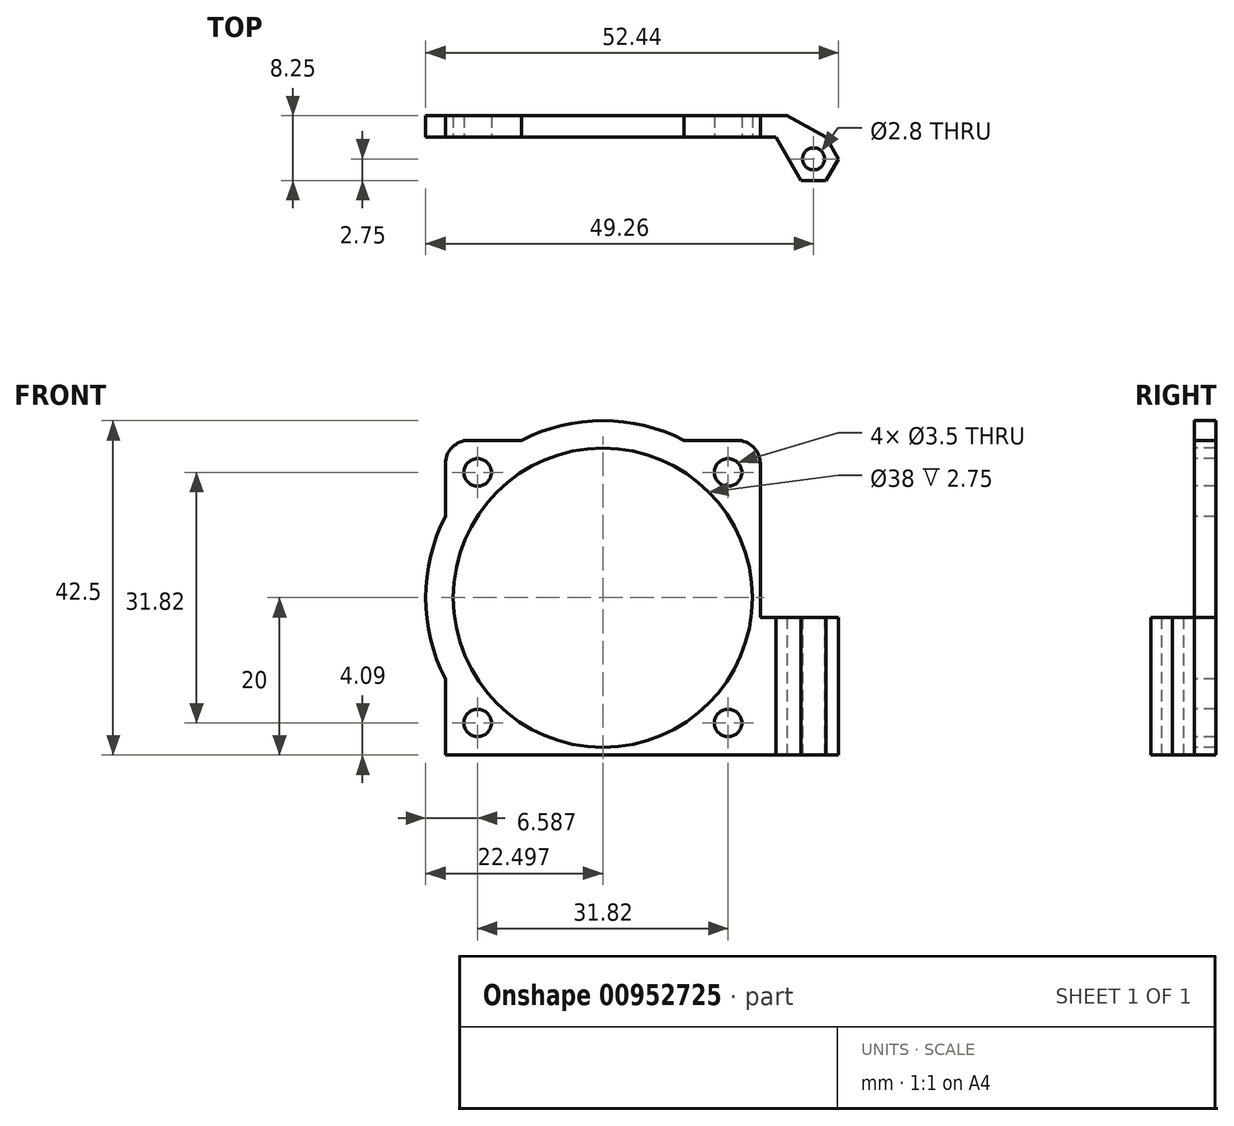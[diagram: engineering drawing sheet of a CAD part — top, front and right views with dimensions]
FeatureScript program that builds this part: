
annotation { "Feature Type Name" : "Feature", "Feature Type Description" : "" }
export const myFeature = defineFeature(function(context is Context, id is Id, definition is map)
    precondition{}
    {
        {
            var Q0;
            Q0=qCreatedBy(makeId("Top.planeOp"),FACE);
            var sketch = newSketch(context, id + "F0", { "sketchPlane" : qUnion([Q0])});
            skCircle(sketch, "E0", {"center": v(0, 0) * mm, "radius": 2.75 * mm, "construction": true});
            skCircle(sketch, "E1", {"center": v(0, 0) * mm, "radius": 1.4 * mm});
            skLineSegment(sketch, "E2.0", {"start": v(1.59, -2.75) * mm, "end": v(-1.59, -2.75) * mm});
            skLineSegment(sketch, "E2.2", {"start": v(-3.18, 0) * mm, "end": v(-1.59, 2.75) * mm, "construction": true});
            skLineSegment(sketch, "E2.3", {"start": v(-1.59, 2.75) * mm, "end": v(1.59, 2.75) * mm, "construction": true});
            skPoint(sketch, "E2.0.midPoint", {"position": v(0, -2.75) * mm});
            skLineSegment(sketch, "E3.bottom", {"start": v(1.59, 2.75) * mm, "end": v(-1.59, 2.75) * mm});
            skLineSegment(sketch, "E3.top", {"start": v(-3.35, 5.5) * mm, "end": v(-46.76, 5.5) * mm});
            skLineSegment(sketch, "E3.right", {"start": v(-46.76, 2.75) * mm, "end": v(-46.76, 5.5) * mm});
            skLineSegment(sketch, "E4", {"start": v(-3.18, 0) * mm, "end": v(-1.59, -2.75) * mm});
            skLineSegment(sketch, "E5.trimOffspring", {"start": v(-4.76, 2.75) * mm, "end": v(-46.76, 2.75) * mm});
            skPoint(sketch, "E6", {"position": v(3.18, 0) * mm});
            skLineSegment(sketch, "E7", {"start": v(1.59, -2.75) * mm, "end": v(3.18, 0) * mm});
            skLineSegment(sketch, "E8", {"start": v(3.18, 0) * mm, "end": v(1.59, 2.75) * mm});
            skLineSegment(sketch, "E9", {"start": v(-4.76, 2.75) * mm, "end": v(-3.18, 0) * mm});
            skLineSegment(sketch, "E10", {"start": v(-3.35, 5.5) * mm, "end": v(1.59, 2.75) * mm});
            skSolve(sketch);
        }
        {
            var Q0;
            Q0=makeQuery(id+"F0.imprint","IMPRINT",FACE,{"disambiguationData":[TD([[makeQuery(id+"F0.imprint","IMPRINT",EDGE,{"derivedFrom":sQuery(id+"F0.wireOp",EDGE,"E1")}),-1.0]])]});
            extrude(context, id + "F1", {"entities" : qUnion([Q0]), "depth" : 40 * mm, "offsetDistance" : 25 * mm});
        }
        {
            var Q0;
            Q0=makeQuery(id+"F1.opExtrude","SWEPT_FACE",FACE,{"disambiguationData":[OSD([sQuery(id+"F0.wireOp",EDGE,"E3.top")])]});
            var sketch = newSketch(context, id + "F2", { "sketchPlane" : qUnion([Q0])});
            skLineSegment(sketch, "E11.bottom", {"start": v(-4.18, 40.83) * mm, "end": v(6.76, 40.83) * mm});
            skLineSegment(sketch, "E11.top", {"start": v(-4.18, 17.5) * mm, "end": v(6.76, 17.5) * mm});
            skLineSegment(sketch, "E11.left", {"start": v(-4.18, 40.83) * mm, "end": v(-4.18, 17.5) * mm});
            skLineSegment(sketch, "E11.right", {"start": v(6.76, 40.83) * mm, "end": v(6.76, 17.5) * mm});
            skSolve(sketch);
        }
        {
            var Q0;
            {var subQ1=sQuery(id+"F2.wireOp",EDGE,"E11.bottom");Q0=makeQuery(id+"F2.imprint","IMPRINT",FACE,{"disambiguationData":[TD([[makeQuery(id+"F2.imprint","IMPRINT",EDGE,{"derivedFrom":subQ1}),-1.0]])]});}
            var Q1;
            {var subQ0=sQuery(id+"F2.wireOp",EDGE,"E11.right");var subQ1=sQuery(id+"F2.wireOp",EDGE,"E11.top");var subQ2=makeQuery(id+"F2.imprint","INTERSECT",VERTEX,{"derivedFrom":[subQ1,subQ0]});Q1=makeQuery(id+"F2.imprint","IMPRINT",FACE,{"disambiguationData":[TD([[makeQuery(id+"F2.imprint","IMPRINT",EDGE,{"disambiguationData":[TD([[subQ2,1.0]])],"derivedFrom":subQ0}),-1.0]])]});}
            extrude(context, id + "F3", {"entities" : qUnion([Q0, Q1]), "operationType" : NewBodyOperationType.REMOVE, "oppositeDirection" : true, "depth" : 25 * mm, "offsetDistance" : 25 * mm});
        }
        {
            var Q0;
            Q0=makeQuery(id+"F1.opExtrude","SWEPT_FACE",FACE,{"disambiguationData":[OSD([sQuery(id+"F0.wireOp",EDGE,"E5.trimOffspring")])]});
            var sketch = newSketch(context, id + "F4", { "sketchPlane" : qUnion([Q0])});
            skLineSegment(sketch, "E12.bottom", {"start": v(-43.76, 40) * mm, "end": v(-9.76, 40) * mm});
            skLineSegment(sketch, "E12.top", {"start": v(-43.76, 0) * mm, "end": v(-6.76, 0) * mm});
            skLineSegment(sketch, "E12.left", {"start": v(-46.76, 37) * mm, "end": v(-46.76, 9.7) * mm});
            skLineSegment(sketch, "E12.right", {"start": v(-6.76, 37) * mm, "end": v(-6.76, 0) * mm});
            skLineSegment(sketch, "E13", {"start": v(-6.76, 40) * mm, "end": v(-46.76, 0) * mm, "construction": true});
            skLineSegment(sketch, "E14", {"start": v(-46.76, 40) * mm, "end": v(-6.76, 0) * mm, "construction": true});
            skCircle(sketch, "E15", {"center": v(-10.85, 4.1) * mm, "radius": 1.75 * mm});
            skCircle(sketch, "E16", {"center": v(-42.67, 35.9) * mm, "radius": 1.75 * mm});
            skCircle(sketch, "E17", {"center": v(-42.67, 4.1) * mm, "radius": 1.75 * mm});
            skCircle(sketch, "E18", {"center": v(-10.85, 35.9) * mm, "radius": 1.75 * mm});
            skCircle(sketch, "E19", {"center": v(-26.76, 20) * mm, "radius": 19 * mm});
            skArc(sketch, "E20", {"start": v(-16.46, 40) * mm, "mid": v(-26.76, 42.5) * mm, "end": v(-37.07, 40) * mm});
            skArc(sketch, "E21", {"start": v(-37.07, 40) * mm, "mid": v(-42.67, 35.9) * mm, "end": v(-46.76, 30.3) * mm, "construction": true});
            skArc(sketch, "E22", {"start": v(-46.76, 30.3) * mm, "mid": v(-49.26, 20) * mm, "end": v(-46.76, 9.7) * mm});
            skLineSegment(sketch, "E23", {"start": v(-46.76, 9.7) * mm, "end": v(-46.76, 3) * mm});
            skArc(sketch, "E24", {"start": v(-46.76, 9.7) * mm, "mid": v(-10.85, 4.1) * mm, "end": v(-16.46, 40) * mm, "construction": true});
            skLineSegment(sketch, "E25", {"start": v(-46.76, 9.7) * mm, "end": v(-46.76, 9.7) * mm});
            skPoint(sketch, "E26.visualSharp", {"position": v(-6.76, 40) * mm});
            skArc(sketch, "E26.filletArc", {"start": v(-6.76, 37) * mm, "mid": v(-7.64, 39.12) * mm, "end": v(-9.76, 40) * mm});
            skPoint(sketch, "E27.visualSharp", {"position": v(-46.76, 40) * mm});
            skArc(sketch, "E27.filletArc", {"start": v(-43.76, 40) * mm, "mid": v(-45.88, 39.12) * mm, "end": v(-46.76, 37) * mm});
            skPoint(sketch, "E28.visualSharp", {"position": v(-46.76, 0) * mm});
            skArc(sketch, "E28.filletArc", {"start": v(-46.76, 3) * mm, "mid": v(-45.88, 0.88) * mm, "end": v(-43.76, 0) * mm});
            skSolve(sketch);
        }
        {
            var Q0;
            {var subQ0=sQuery(id+"F4.wireOp",EDGE,"E22");Q0=makeQuery(id+"F4.imprint","IMPRINT",FACE,{"disambiguationData":[TD([[makeQuery(id+"F4.imprint","IMPRINT",EDGE,{"derivedFrom":subQ0}),1.0]])]});}
            var Q1;
            {var subQ0=sQuery(id+"F4.wireOp",EDGE,"E20");Q1=makeQuery(id+"F4.imprint","IMPRINT",FACE,{"disambiguationData":[TD([[makeQuery(id+"F4.imprint","IMPRINT",EDGE,{"derivedFrom":subQ0}),1.0]])]});}
            extrude(context, id + "F5", {"entities" : qUnion([Q0, Q1]), "operationType" : NewBodyOperationType.ADD, "oppositeDirection" : true, "depth" : 2.75 * mm, "offsetDistance" : 25 * mm});
        }
        {
            var Q0;
            {var subQ0=sQuery(id+"F4.wireOp",EDGE,"E26.filletArc");Q0=makeQuery(id+"F4.imprint","IMPRINT",FACE,{"disambiguationData":[TD([[makeQuery(id+"F4.imprint","IMPRINT",EDGE,{"derivedFrom":subQ0}),-1.0]])]});}
            var Q1;
            {var subQ0=sQuery(id+"F4.wireOp",EDGE,"E27.filletArc");Q1=makeQuery(id+"F4.imprint","IMPRINT",FACE,{"disambiguationData":[TD([[makeQuery(id+"F4.imprint","IMPRINT",EDGE,{"derivedFrom":subQ0}),-1.0]])]});}
            var Q2;
            Q2=makeQuery(id+"F4.imprint","IMPRINT",FACE,{"disambiguationData":[TD([[makeQuery(id+"F4.imprint","IMPRINT",EDGE,{"derivedFrom":sQuery(id+"F4.wireOp",EDGE,"E16")}),1.0]])]});
            var Q3;
            Q3=makeQuery(id+"F4.imprint","IMPRINT",FACE,{"disambiguationData":[TD([[makeQuery(id+"F4.imprint","IMPRINT",EDGE,{"derivedFrom":sQuery(id+"F4.wireOp",EDGE,"E17")}),1.0]])]});
            var Q4;
            Q4=makeQuery(id+"F4.imprint","IMPRINT",FACE,{"disambiguationData":[TD([[makeQuery(id+"F4.imprint","IMPRINT",EDGE,{"derivedFrom":sQuery(id+"F4.wireOp",EDGE,"E15")}),1.0]])]});
            var Q5;
            Q5=makeQuery(id+"F4.imprint","IMPRINT",FACE,{"disambiguationData":[TD([[makeQuery(id+"F4.imprint","IMPRINT",EDGE,{"derivedFrom":sQuery(id+"F4.wireOp",EDGE,"E18")}),1.0]])]});
            var Q6;
            Q6=makeQuery(id+"F4.imprint","IMPRINT",FACE,{"disambiguationData":[TD([[makeQuery(id+"F4.imprint","IMPRINT",EDGE,{"derivedFrom":sQuery(id+"F4.wireOp",EDGE,"E19")}),1.0]])]});
            extrude(context, id + "F6", {"entities" : qUnion([Q0, Q1, Q2, Q3, Q4, Q5, Q6]), "operationType" : NewBodyOperationType.REMOVE, "oppositeDirection" : true, "depth" : 25 * mm, "offsetDistance" : 25 * mm});
        }
    });
